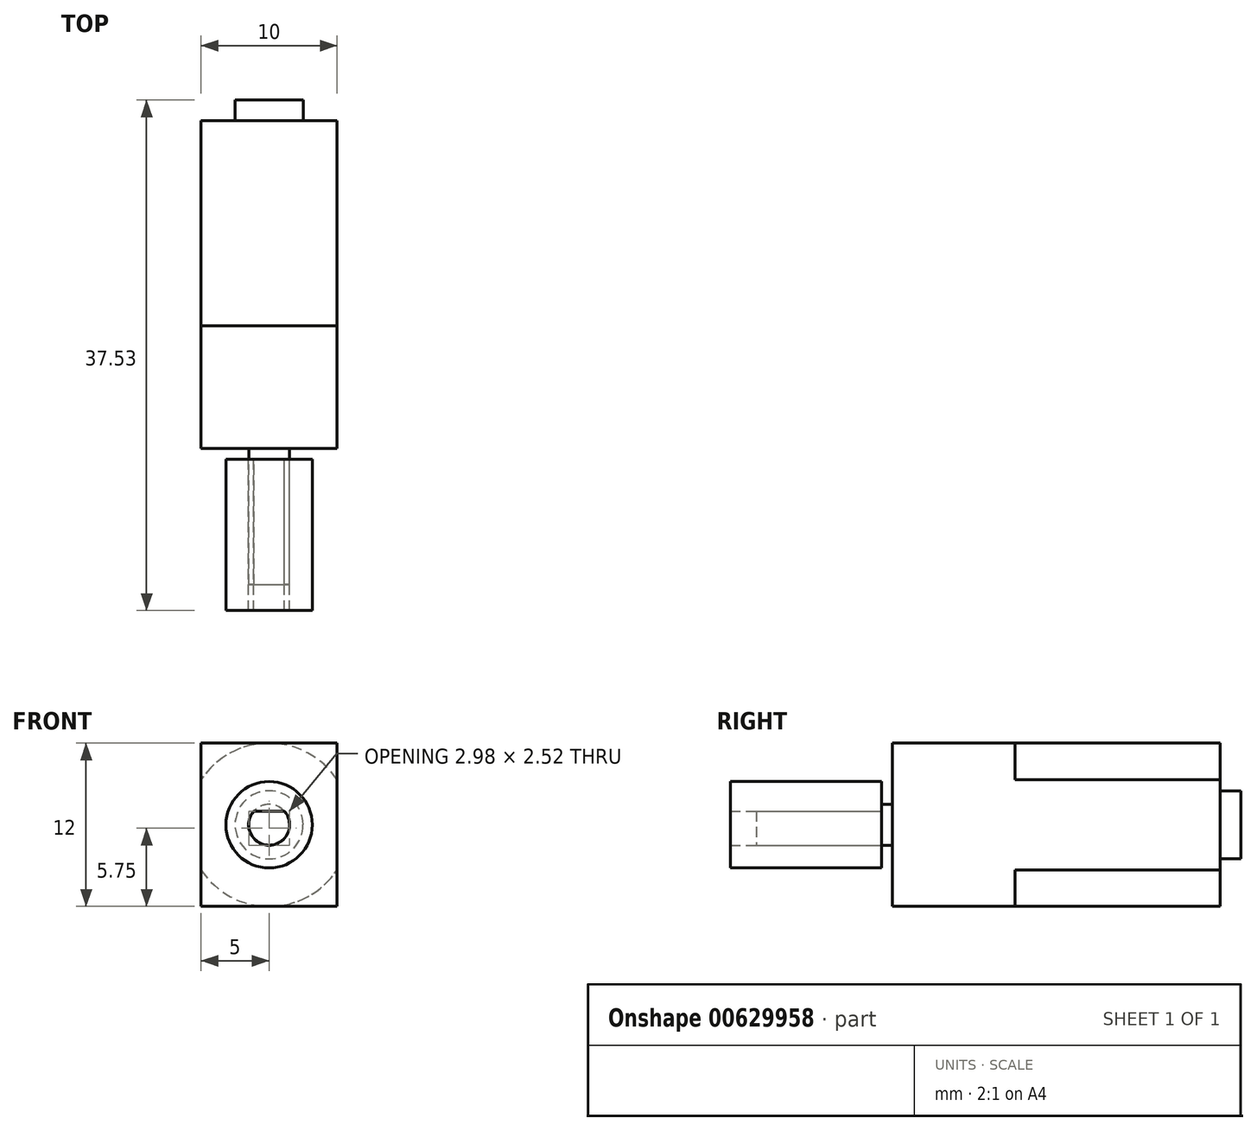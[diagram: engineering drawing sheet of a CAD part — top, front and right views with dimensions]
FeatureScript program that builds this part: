
annotation { "Feature Type Name" : "Feature", "Feature Type Description" : "" }
export const myFeature = defineFeature(function(context is Context, id is Id, definition is map)
    precondition{}
    {
        {
            var Q0;
            Q0=qCreatedBy(makeId("Front.planeOp"),FACE);
            var sketch = newSketch(context, id + "F0", { "sketchPlane" : qUnion([Q0])});
            skArc(sketch, "E0", {"start": v(5, 3.32) * mm, "mid": v(0, 6) * mm, "end": v(-5, 3.32) * mm});
            skLineSegment(sketch, "E1", {"start": v(-5, 3.32) * mm, "end": v(-5, -3.32) * mm});
            skLineSegment(sketch, "E2", {"start": v(5, -3.32) * mm, "end": v(5, 3.32) * mm});
            skArc(sketch, "E3.trimOffspring", {"start": v(-5, -3.32) * mm, "mid": v(0, -6) * mm, "end": v(5, -3.32) * mm});
            skSolve(sketch);
        }
        {
            var Q0;
            Q0 = qSketchRegion(id + "F0", true);
            extrude(context, id + "F1", {"entities" : qUnion([Q0]), "oppositeDirection" : true, "depth" : 9 * mm + 15.1 * mm, "offsetDistance" : 25.4 * mm});
        }
        {
            var Q0;
            Q0=qCreatedBy(makeId("Front.planeOp"),FACE);
            var sketch = newSketch(context, id + "F2", { "sketchPlane" : qUnion([Q0])});
            skLineSegment(sketch, "E4.bottom", {"start": v(5, 6) * mm, "end": v(-5, 6) * mm});
            skLineSegment(sketch, "E4.top", {"start": v(5, -6) * mm, "end": v(-5, -6) * mm});
            skLineSegment(sketch, "E4.left", {"start": v(5, 6) * mm, "end": v(5, -6) * mm});
            skLineSegment(sketch, "E4.right", {"start": v(-5, 6) * mm, "end": v(-5, -6) * mm});
            skPoint(sketch, "E4.middle", {"position": v(0, 0) * mm});
            skSolve(sketch);
        }
        {
            var Q0;
            Q0 = qSketchRegion(id + "F2", true);
            extrude(context, id + "F3", {"entities" : qUnion([Q0]), "operationType" : NewBodyOperationType.ADD, "oppositeDirection" : true, "depth" : 9 * mm, "offsetDistance" : 25.4 * mm});
        }
        {
            var Q0;
            Q0=makeQuery(id+"F3.boolean.opBoolean","MERGE",FACE,{"derivedFrom":[makeQuery(id+"F1.opExtrude","CAP_FACE",FACE,{"disambiguationData":[OSD([sQuery(id+"F0.wireOp",EDGE,"E0"),sQuery(id+"F0.wireOp",EDGE,"E1"),sQuery(id+"F0.wireOp",EDGE,"E2"),sQuery(id+"F0.wireOp",EDGE,"E3.trimOffspring")])],"isStart":true}),makeQuery(id+"F3.opExtrude","CAP_FACE",FACE,{"disambiguationData":[OSD([sQuery(id+"F2.wireOp",EDGE,"E4.bottom"),sQuery(id+"F2.wireOp",EDGE,"E4.top"),sQuery(id+"F2.wireOp",EDGE,"E4.left"),sQuery(id+"F2.wireOp",EDGE,"E4.right")])],"isStart":true})]});
            var sketch = newSketch(context, id + "F4", { "sketchPlane" : qUnion([Q0])});
            skArc(sketch, "E5", {"start": v(-1.12, 1) * mm, "mid": v(0, -1.5) * mm, "end": v(1.12, 1) * mm});
            skPoint(sketch, "E6.endSnap0", {"position": v(-5, 0) * mm});
            skLineSegment(sketch, "E7", {"start": v(-1.12, 1) * mm, "end": v(1.12, 1) * mm});
            skSolve(sketch);
        }
        {
            var Q0;
            Q0 = qSketchRegion(id + "F4", true);
            extrude(context, id + "F5", {"entities" : qUnion([Q0]), "operationType" : NewBodyOperationType.ADD, "depth" : 10 * mm, "offsetDistance" : 25.4 * mm});
        }
        {
            var Q0;
            Q0=makeQuery(id+"F1.opExtrude","CAP_FACE",FACE,{"disambiguationData":[OSD([sQuery(id+"F0.wireOp",EDGE,"E0"),sQuery(id+"F0.wireOp",EDGE,"E1"),sQuery(id+"F0.wireOp",EDGE,"E2"),sQuery(id+"F0.wireOp",EDGE,"E3.trimOffspring")])],"isStart":false});
            var sketch = newSketch(context, id + "F6", { "sketchPlane" : qUnion([Q0])});
            skCircle(sketch, "E8", {"center": v(0, 0) * mm, "radius": 2.5 * mm});
            skSolve(sketch);
        }
        {
            var Q0;
            Q0 = qSketchRegion(id + "F6", true);
            extrude(context, id + "F7", {"entities" : qUnion([Q0]), "operationType" : NewBodyOperationType.ADD, "depth" : 1.5 * mm, "offsetDistance" : 25.4 * mm});
        }
        {
            var Q0;
            Q0=makeQuery(id+"F3.boolean.opBoolean","MERGE",FACE,{"derivedFrom":[makeQuery(id+"F1.opExtrude","CAP_FACE",FACE,{"disambiguationData":[OSD([sQuery(id+"F0.wireOp",EDGE,"E0"),sQuery(id+"F0.wireOp",EDGE,"E1"),sQuery(id+"F0.wireOp",EDGE,"E2"),sQuery(id+"F0.wireOp",EDGE,"E3.trimOffspring")])],"isStart":true}),makeQuery(id+"F3.opExtrude","CAP_FACE",FACE,{"disambiguationData":[OSD([sQuery(id+"F2.wireOp",EDGE,"E4.bottom"),sQuery(id+"F2.wireOp",EDGE,"E4.top"),sQuery(id+"F2.wireOp",EDGE,"E4.left"),sQuery(id+"F2.wireOp",EDGE,"E4.right")])],"isStart":true})]});
            var sketch = newSketch(context, id + "F8", { "sketchPlane" : qUnion([Q0])});
            skCircle(sketch, "E9", {"center": v(0, 0) * mm, "radius": 1.5 * mm});
            skSolve(sketch);
        }
        {
            var Q0;
            Q0 = qSketchRegion(id + "F8", true);
            extrude(context, id + "F9", {"entities" : qUnion([Q0]), "operationType" : NewBodyOperationType.ADD, "depth" : .8 * mm, "offsetDistance" : 25.4 * mm});
        }
        {
            var Q0;
            Q0=makeQuery(id+"F9.opExtrude","CAP_FACE",FACE,{"disambiguationData":[OSD([sQuery(id+"F8.wireOp",EDGE,"E9")])],"isStart":false});
            var sketch = newSketch(context, id + "F10", { "sketchPlane" : qUnion([Q0])});
            skCircle(sketch, "E10", {"center": v(0, 0) * mm, "radius": 3.18 * mm});
            skArc(sketch, "E11.0", {"start": v(-1.12, 1) * mm, "mid": v(0, -1.5) * mm, "end": v(1.12, 1) * mm});
            skLineSegment(sketch, "E11.1", {"start": v(-1.12, 1) * mm, "end": v(1.12, 1) * mm});
            skSolve(sketch);
        }
        {
            var Q0;
            Q0 = qSketchRegion(id + "F10", true);
            extrude(context, id + "F11", {"entities" : qUnion([Q0]), "depth" : 11.13 * mm, "offsetDistance" : 25.4 * mm});
        }
    });
